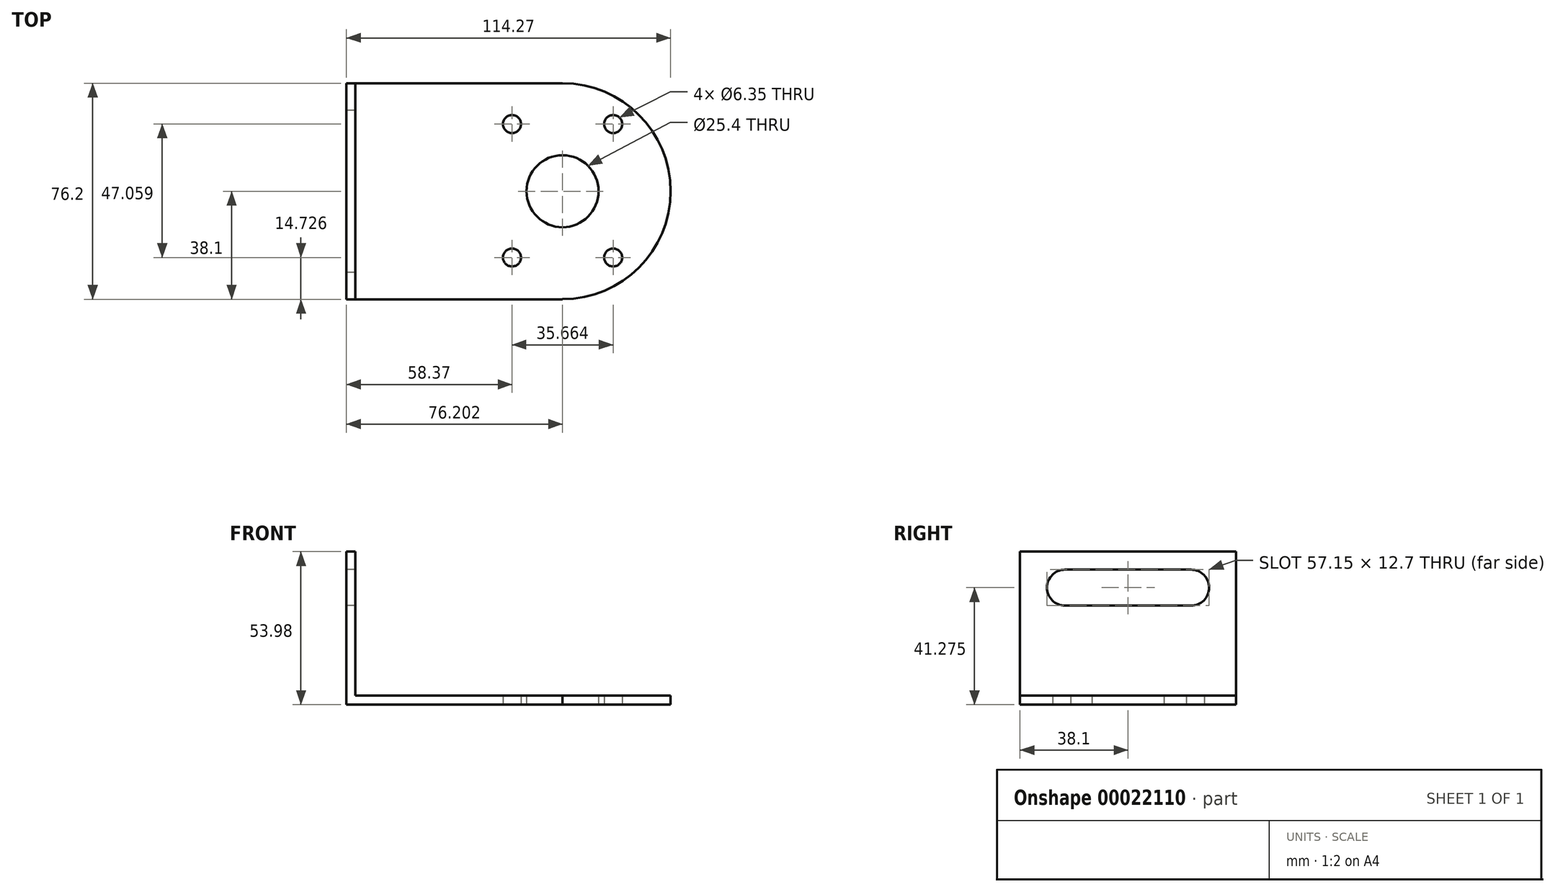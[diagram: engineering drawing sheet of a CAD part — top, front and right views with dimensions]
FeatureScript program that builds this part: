
annotation { "Feature Type Name" : "Feature", "Feature Type Description" : "" }
export const myFeature = defineFeature(function(context is Context, id is Id, definition is map)
    precondition{}
    {
        {
            var Q0;
            Q0=qCreatedBy(makeId("Top.planeOp"),FACE);
            var sketch = newSketch(context, id + "F0", { "sketchPlane" : qUnion([Q0])});
            skLineSegment(sketch, "E0.bottom", {"start": v(-58.37, 43.01) * mm, "end": v(17.83, 43.01) * mm});
            skLineSegment(sketch, "E0.top", {"start": v(-58.37, -33.19) * mm, "end": v(17.83, -33.19) * mm});
            skLineSegment(sketch, "E0.left", {"start": v(-58.37, 43.01) * mm, "end": v(-58.37, -33.19) * mm});
            skLineSegment(sketch, "E0.right", {"start": v(17.83, 43.01) * mm, "end": v(17.83, -33.19) * mm});
            skCircle(sketch, "E1", {"center": v(17.83, 4.91) * mm, "radius": 38.07 * mm});
            skCircle(sketch, "E2", {"center": v(17.83, 4.91) * mm, "radius": 12.7 * mm});
            skCircle(sketch, "E3", {"center": v(17.83, 5.07) * mm, "radius": 29.52 * mm, "construction": true});
            skCircle(sketch, "E4", {"center": v(0, 28.6) * mm, "radius": 3.18 * mm});
            skCircle(sketch, "E5", {"center": v(0, -18.46) * mm, "radius": 3.18 * mm});
            skCircle(sketch, "E6", {"center": v(35.66, 28.6) * mm, "radius": 3.18 * mm});
            skCircle(sketch, "E7", {"center": v(35.66, -18.46) * mm, "radius": 3.18 * mm});
            skSolve(sketch);
        }
        {
            var sketch = newSketch(context, id + "F1", { "sketchPlane" : qUnion([])});
            skLineSegment(sketch, "E8", {"start": v(-54.82, 42.84) * mm, "end": v(-54.82, -33.06) * mm});
            skSolve(sketch);
        }
        {
            var Q0;
            Q0 = qSketchRegion(id + "F1", true);
            var Q1;
            {var subQ4=sQuery(id+"F0.wireOp",EDGE,"E0.bottom");Q1=makeQuery(id+"F0.imprint","IMPRINT",FACE,{"disambiguationData":[TD([[makeQuery(id+"F0.imprint","IMPRINT",EDGE,{"derivedFrom":subQ4}),-1.0]])]});}
            var Q2;
            Q2=makeQuery(id+"F0.imprint","IMPRINT",FACE,{"disambiguationData":[TD([[makeQuery(id+"F0.imprint","IMPRINT",EDGE,{"derivedFrom":sQuery(id+"F0.wireOp",EDGE,"E4")}),-1.0]])]});
            var Q3;
            Q3=makeQuery(id+"F0.imprint","IMPRINT",FACE,{"disambiguationData":[TD([[makeQuery(id+"F0.imprint","IMPRINT",EDGE,{"derivedFrom":sQuery(id+"F0.wireOp",EDGE,"E6")}),-1.0]])]});
            extrude(context, id + "F2", {"entities" : qUnion([Q0, Q1, Q2, Q3]), "depth" : 3.17 * mm});
        }
        {
            var Q0;
            Q0=makeQuery(id+"F2.opExtrude","CAP_FACE",FACE,{"disambiguationData":[OSD([sQuery(id+"F0.wireOp",EDGE,"E0.bottom"),sQuery(id+"F0.wireOp",EDGE,"E0.top"),sQuery(id+"F0.wireOp",EDGE,"E0.left"),sQuery(id+"F0.wireOp",EDGE,"E0.right"),sQuery(id+"F0.wireOp",EDGE,"E1"),sQuery(id+"F0.wireOp",EDGE,"E2"),sQuery(id+"F0.wireOp",EDGE,"E4"),sQuery(id+"F0.wireOp",EDGE,"E5"),sQuery(id+"F0.wireOp",EDGE,"E6"),sQuery(id+"F0.wireOp",EDGE,"E7")])],"isStart":false});
            var sketch = newSketch(context, id + "F3", { "sketchPlane" : qUnion([Q0])});
            skLineSegment(sketch, "E9.bottom", {"start": v(-58.37, 43.01) * mm, "end": v(-55.2, 43.01) * mm});
            skLineSegment(sketch, "E9.top", {"start": v(-58.37, -33.19) * mm, "end": v(-55.2, -33.19) * mm});
            skLineSegment(sketch, "E9.left", {"start": v(-58.37, 43.01) * mm, "end": v(-58.37, -33.19) * mm});
            skLineSegment(sketch, "E9.right", {"start": v(-55.2, 43.01) * mm, "end": v(-55.2, -33.19) * mm});
            skSolve(sketch);
        }
        {
            var Q0;
            Q0 = qSketchRegion(id + "F3", true);
            extrude(context, id + "F4", {"entities" : qUnion([Q0]), "operationType" : NewBodyOperationType.ADD, "depth" : 50.8 * mm});
        }
        {
            var Q0;
            Q0=makeQuery(id+"F4.boolean.opBoolean","MERGE",FACE,{"derivedFrom":[makeQuery(id+"F2.opExtrude","SWEPT_FACE",FACE,{"disambiguationData":[OSD([sQuery(id+"F0.wireOp",EDGE,"E0.left")])]}),makeQuery(id+"F4.opExtrude","SWEPT_FACE",FACE,{"disambiguationData":[OSD([sQuery(id+"F3.wireOp",EDGE,"E9.left")])]})]});
            var sketch = newSketch(context, id + "F5", { "sketchPlane" : qUnion([Q0])});
            skLineSegment(sketch, "E10.rect.bottom", {"start": v(-27.14, 34.93) * mm, "end": v(17.31, 34.93) * mm});
            skLineSegment(sketch, "E10.rect.top", {"start": v(-27.14, 47.63) * mm, "end": v(17.31, 47.63) * mm});
            skPoint(sketch, "E10.rect.middle", {"position": v(-4.91, 41.27) * mm});
            skArc(sketch, "E11", {"start": v(-27.14, 47.63) * mm, "mid": v(-33.49, 41.28) * mm, "end": v(-27.14, 34.93) * mm});
            skArc(sketch, "E12", {"start": v(17.31, 34.92) * mm, "mid": v(23.66, 41.28) * mm, "end": v(17.31, 47.63) * mm});
            skSolve(sketch);
        }
        {
            var Q0;
            Q0 = qSketchRegion(id + "F5", true);
            extrude(context, id + "F6", {"entities" : qUnion([Q0]), "operationType" : NewBodyOperationType.REMOVE, "oppositeDirection" : true, "depth" : 25.4 * mm});
        }
    });
